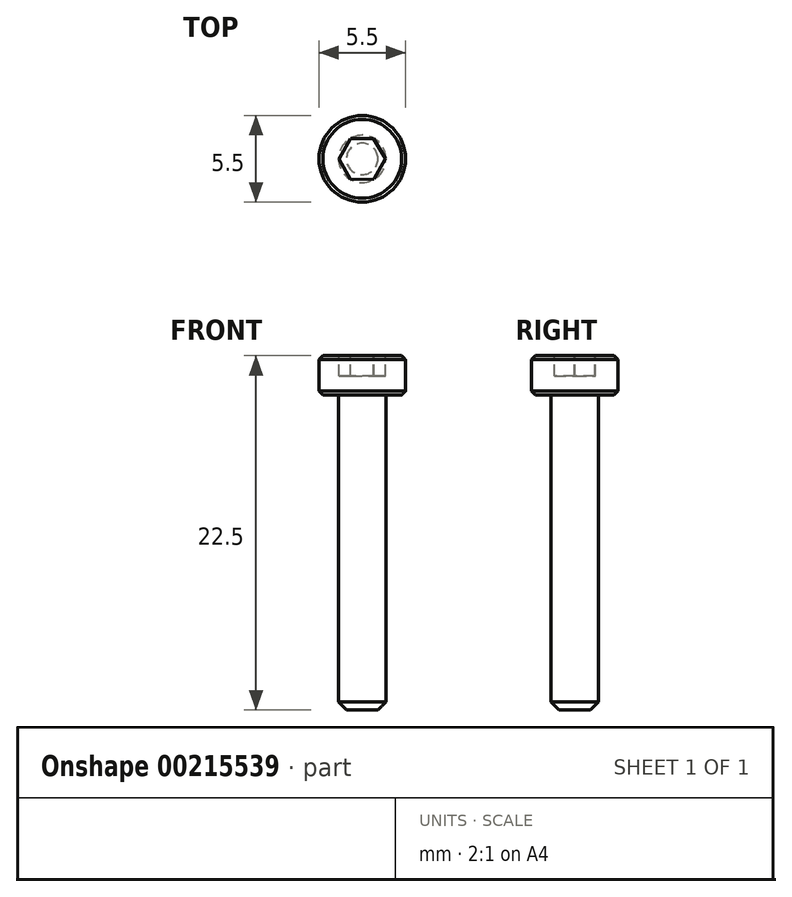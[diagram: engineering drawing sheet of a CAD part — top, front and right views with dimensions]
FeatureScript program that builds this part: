
annotation { "Feature Type Name" : "Feature", "Feature Type Description" : "" }
export const myFeature = defineFeature(function(context is Context, id is Id, definition is map)
    precondition{}
    {
        {
            var Q0;
            Q0=qCreatedBy(makeId("Top.planeOp"),FACE);
            var sketch = newSketch(context, id + "F0", { "sketchPlane" : qUnion([Q0])});
            skCircle(sketch, "E0", {"center": v(0, 0) * mm, "radius": 1.5 * mm});
            skCircle(sketch, "E1", {"center": v(0, 0) * mm, "radius": 2.75 * mm});
            skSolve(sketch);
        }
        {
            var Q0;
            Q0=makeQuery(id+"F0.imprint","IMPRINT",FACE,{"disambiguationData":[TD([[makeQuery(id+"F0.imprint","IMPRINT",EDGE,{"derivedFrom":sQuery(id+"F0.wireOp",EDGE,"E0")}),1.0]])]});
            extrude(context, id + "F1", {"entities" : qUnion([Q0]), "oppositeDirection" : true, "depth" : 20 * mm});
        }
        {
            var Q0;
            Q0=makeQuery(id+"F1.opExtrude","CAP_EDGE",EDGE,{"disambiguationData":[OSD([sQuery(id+"F0.wireOp",EDGE,"E0")])],"isStart":false});
            chamfer(context, id + "F2", {"entities" : qUnion([Q0]), "width" : .5 * mm, "tangentPropagation" : true});
        }
        {
            var Q0;
            Q0=makeQuery(id+"F0.imprint","IMPRINT",FACE,{"disambiguationData":[TD([[makeQuery(id+"F0.imprint","IMPRINT",EDGE,{"derivedFrom":sQuery(id+"F0.wireOp",EDGE,"E0")}),-1.0]])]});
            var Q1;
            Q1=makeQuery(id+"F0.imprint","IMPRINT",FACE,{"disambiguationData":[TD([[makeQuery(id+"F0.imprint","IMPRINT",EDGE,{"derivedFrom":sQuery(id+"F0.wireOp",EDGE,"E0")}),1.0]])]});
            extrude(context, id + "F3", {"entities" : qUnion([Q0, Q1]), "operationType" : NewBodyOperationType.ADD, "depth" : 2.5 * mm});
        }
        {
            var Q0;
            Q0=makeQuery(id+"F3.opExtrude","CAP_FACE",FACE,{"disambiguationData":[OSD([sQuery(id+"F0.wireOp",EDGE,"E1")])],"isStart":false});
            var Q1;
            Q1=makeQuery(id+"F3.opExtrude","CAP_EDGE",EDGE,{"disambiguationData":[OSD([sQuery(id+"F0.wireOp",EDGE,"E1")])],"isStart":true});
            chamfer(context, id + "F4", {"entities" : qUnion([Q0, Q1]), "width" : .25 * mm, "tangentPropagation" : true});
        }
        {
            var Q0;
            Q0=makeQuery(id+"F3.opExtrude","CAP_FACE",FACE,{"disambiguationData":[OSD([sQuery(id+"F0.wireOp",EDGE,"E1")])],"isStart":false});
            var sketch = newSketch(context, id + "F5", { "sketchPlane" : qUnion([Q0])});
            skCircle(sketch, "E2.cCircle", {"center": v(0, 0) * mm, "radius": 1.29 * mm, "construction": true});
            skLineSegment(sketch, "E2.0", {"start": v(1.49, 0.02) * mm, "end": v(0.76, -1.28) * mm});
            skLineSegment(sketch, "E2.1", {"start": v(0.76, -1.28) * mm, "end": v(-0.73, -1.3) * mm});
            skLineSegment(sketch, "E2.2", {"start": v(-0.73, -1.3) * mm, "end": v(-1.49, -0.02) * mm});
            skLineSegment(sketch, "E2.3", {"start": v(-1.49, -0.02) * mm, "end": v(-0.76, 1.28) * mm});
            skLineSegment(sketch, "E2.4", {"start": v(-0.76, 1.28) * mm, "end": v(0.73, 1.3) * mm});
            skLineSegment(sketch, "E2.5", {"start": v(0.73, 1.3) * mm, "end": v(1.49, 0.02) * mm});
            skPoint(sketch, "E2.0.midPoint", {"position": v(1.12, -0.63) * mm});
            skSolve(sketch);
        }
        {
            var Q0;
            Q0 = qSketchRegion(id + "F5", true);
            extrude(context, id + "F6", {"entities" : qUnion([Q0]), "operationType" : NewBodyOperationType.REMOVE, "oppositeDirection" : true, "depth" : 1.3 * mm});
        }
    });
